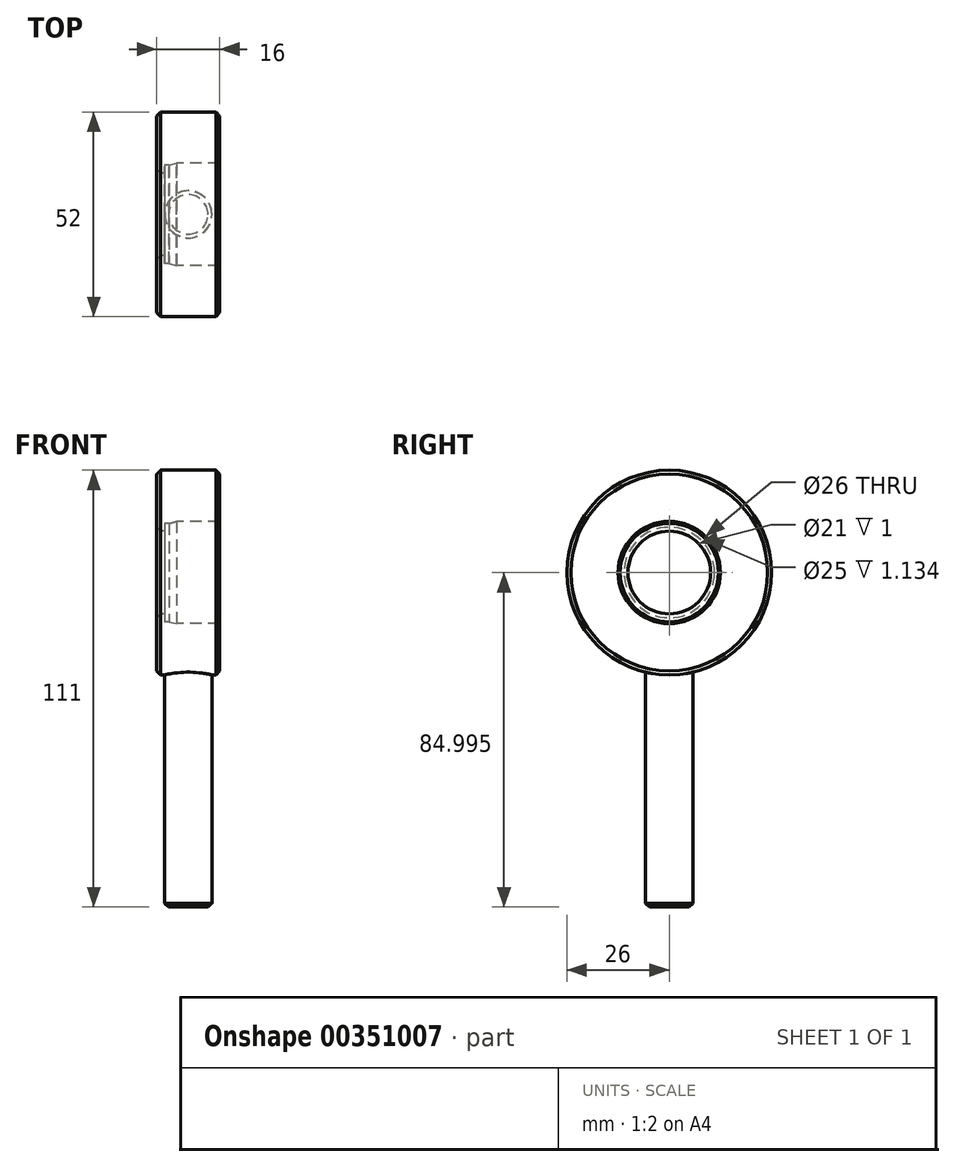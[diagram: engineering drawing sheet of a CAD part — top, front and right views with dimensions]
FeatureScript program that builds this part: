
annotation { "Feature Type Name" : "Feature", "Feature Type Description" : "" }
export const myFeature = defineFeature(function(context is Context, id is Id, definition is map)
    precondition{}
    {
        {
            var Q0;
            Q0=qCreatedBy(makeId("Front.planeOp"),FACE);
            var sketch = newSketch(context, id + "F0", { "sketchPlane" : qUnion([Q0])});
            skLineSegment(sketch, "E0", {"start": v(70.14, -4.23) * mm, "end": v(70.14, 46.77) * mm});
            skLineSegment(sketch, "E1", {"start": v(69.14, 45.77) * mm, "end": v(69.14, -4.23) * mm});
            skLineSegment(sketch, "E2", {"start": v(85.14, -4.23) * mm, "end": v(85.14, 45.77) * mm});
            skLineSegment(sketch, "E3", {"start": v(84.14, 46.77) * mm, "end": v(84.14, -4.23) * mm});
            skArc(sketch, "E4", {"start": v(29.78, -4.23) * mm, "mid": v(22.64, 46.77) * mm, "end": v(15.5, -4.23) * mm});
            skCircle(sketch, "E5", {"center": v(22.64, 20.77) * mm, "radius": 25 * mm});
            skLineSegment(sketch, "E6", {"start": v(22.64, -68.3) * mm, "end": v(22.64, 49.96) * mm});
            skLineSegment(sketch, "E7", {"start": v(-39.86, -4.23) * mm, "end": v(-39.86, 45.77) * mm});
            skLineSegment(sketch, "E8", {"start": v(-23.86, 45.77) * mm, "end": v(-23.86, -4.23) * mm});
            skArc(sketch, "E9", {"start": v(-79.22, -4.23) * mm, "mid": v(-86.36, 46.77) * mm, "end": v(-93.5, -4.23) * mm});
            skCircle(sketch, "E10", {"center": v(-86.36, 20.77) * mm, "radius": 25 * mm});
            skLineSegment(sketch, "E11", {"start": v(-86.36, -68.3) * mm, "end": v(-86.36, 50.51) * mm});
            skLineSegment(sketch, "E12", {"start": v(-7.6, 20.77) * mm, "end": v(53.07, 20.77) * mm});
            skCircle(sketch, "E13", {"center": v(-86.36, 20.77) * mm, "radius": 11.5 * mm});
            skLineSegment(sketch, "E14", {"start": v(-56.1, 20.77) * mm, "end": v(-117.02, 20.77) * mm});
            skLineSegment(sketch, "E15", {"start": v(-92.36, -63.23) * mm, "end": v(-92.36, -4.23) * mm});
            skLineSegment(sketch, "E16", {"start": v(-80.36, -4.23) * mm, "end": v(-80.36, -63.23) * mm});
            skLineSegment(sketch, "E17", {"start": v(-80.36, -63.23) * mm, "end": v(-81.36, -64.23) * mm});
            skLineSegment(sketch, "E18", {"start": v(-91.36, -64.23) * mm, "end": v(-92.36, -63.23) * mm});
            skLineSegment(sketch, "E19", {"start": v(-81.36, -64.23) * mm, "end": v(-91.36, -64.23) * mm});
            skLineSegment(sketch, "E20", {"start": v(-92.36, -63.23) * mm, "end": v(-80.36, -63.23) * mm});
            skCircle(sketch, "E21", {"center": v(-86.36, 20.77) * mm, "radius": 10.5 * mm});
            skCircle(sketch, "E22", {"center": v(-86.36, -9.23) * mm, "radius": 2 * mm});
            skLineSegment(sketch, "E23", {"start": v(-83.6, -9.23) * mm, "end": v(-89.12, -9.23) * mm});
            skLineSegment(sketch, "E24", {"start": v(-79.22, -4.23) * mm, "end": v(-93.5, -4.23) * mm});
            skLineSegment(sketch, "E25", {"start": v(16.64, -63.23) * mm, "end": v(16.64, -4.23) * mm});
            skLineSegment(sketch, "E26", {"start": v(28.64, -4.23) * mm, "end": v(28.64, -63.23) * mm});
            skLineSegment(sketch, "E27", {"start": v(-37.86, -63.23) * mm, "end": v(-37.86, -4.23) * mm});
            skLineSegment(sketch, "E28", {"start": v(-25.86, -4.23) * mm, "end": v(-25.86, -63.23) * mm});
            skLineSegment(sketch, "E29", {"start": v(-31.86, 2.77) * mm, "end": v(-31.86, -68.3) * mm});
            skLineSegment(sketch, "E30", {"start": v(-26.86, -64.23) * mm, "end": v(-25.86, -63.23) * mm});
            skLineSegment(sketch, "E31", {"start": v(-36.86, -64.23) * mm, "end": v(-26.86, -64.23) * mm});
            skLineSegment(sketch, "E32", {"start": v(-37.86, -63.23) * mm, "end": v(-36.86, -64.23) * mm});
            skLineSegment(sketch, "E33", {"start": v(-25.86, -63.23) * mm, "end": v(-37.86, -63.23) * mm});
            skLineSegment(sketch, "E34", {"start": v(28.64, -63.23) * mm, "end": v(27.64, -64.23) * mm});
            skLineSegment(sketch, "E35", {"start": v(17.64, -64.23) * mm, "end": v(16.64, -63.23) * mm});
            skLineSegment(sketch, "E36", {"start": v(27.64, -64.23) * mm, "end": v(17.64, -64.23) * mm});
            skLineSegment(sketch, "E37", {"start": v(16.64, -63.23) * mm, "end": v(28.64, -63.23) * mm});
            skLineSegment(sketch, "E38", {"start": v(-38.86, 31.27) * mm, "end": v(-38.86, 10.27) * mm});
            skLineSegment(sketch, "E39", {"start": v(-27.86, 33.27) * mm, "end": v(-27.86, 8.27) * mm});
            skLineSegment(sketch, "E40", {"start": v(-37.86, 8.27) * mm, "end": v(-37.86, 33.27) * mm});
            skLineSegment(sketch, "E41", {"start": v(-26.86, 33.77) * mm, "end": v(-26.86, 7.77) * mm});
            skLineSegment(sketch, "E42", {"start": v(-34.86, 7.77) * mm, "end": v(-34.86, 33.77) * mm});
            skLineSegment(sketch, "E43", {"start": v(-36.73, 8.27) * mm, "end": v(-34.86, 7.77) * mm});
            skLineSegment(sketch, "E44", {"start": v(-34.86, 7.77) * mm, "end": v(-26.86, 7.77) * mm});
            skLineSegment(sketch, "E45", {"start": v(-28.86, 0.27) * mm, "end": v(-29.36, 0.77) * mm});
            skLineSegment(sketch, "E46", {"start": v(-29.36, -4.23) * mm, "end": v(-29.36, -3.03) * mm});
            skLineSegment(sketch, "E47", {"start": v(-28.86, -3.03) * mm, "end": v(-28.86, 0.27) * mm});
            skLineSegment(sketch, "E48", {"start": v(-29.36, 0.77) * mm, "end": v(-29.36, -3.03) * mm});
            skLineSegment(sketch, "E49", {"start": v(-34.36, 0.77) * mm, "end": v(-34.86, 0.27) * mm});
            skLineSegment(sketch, "E50", {"start": v(-34.36, -3.03) * mm, "end": v(-34.36, -4.23) * mm});
            skLineSegment(sketch, "E51", {"start": v(-34.86, 0.27) * mm, "end": v(-34.86, -3.03) * mm});
            skLineSegment(sketch, "E52", {"start": v(-34.36, -3.03) * mm, "end": v(-34.36, 0.77) * mm});
            skLineSegment(sketch, "E53", {"start": v(-34.86, -3.03) * mm, "end": v(-28.86, -3.03) * mm});
            skLineSegment(sketch, "E54", {"start": v(-29.36, 0.77) * mm, "end": v(-34.36, 0.77) * mm});
            skLineSegment(sketch, "E55", {"start": v(-28.86, 0.27) * mm, "end": v(-34.86, 0.27) * mm});
            skLineSegment(sketch, "E56", {"start": v(-26.86, 7.77) * mm, "end": v(-23.86, 7.77) * mm});
            skLineSegment(sketch, "E57", {"start": v(-23.86, 9.77) * mm, "end": v(-27.86, 9.77) * mm});
            skLineSegment(sketch, "E58", {"start": v(-26.86, 8.27) * mm, "end": v(-23.86, 8.27) * mm});
            skLineSegment(sketch, "E59", {"start": v(-38.86, 10.27) * mm, "end": v(-37.86, 10.27) * mm});
            skLineSegment(sketch, "E60", {"start": v(-38.86, 10.27) * mm, "end": v(-39.86, 9.27) * mm});
            skLineSegment(sketch, "E61", {"start": v(-23.86, -4.23) * mm, "end": v(-39.86, -4.23) * mm});
            skLineSegment(sketch, "E62", {"start": v(-26.86, 8.27) * mm, "end": v(-37.86, 8.27) * mm});
            skLineSegment(sketch, "E63", {"start": v(-34.86, 33.77) * mm, "end": v(-36.73, 33.27) * mm});
            skLineSegment(sketch, "E64", {"start": v(-26.86, 33.77) * mm, "end": v(-34.86, 33.77) * mm});
            skLineSegment(sketch, "E65", {"start": v(-26.86, 33.77) * mm, "end": v(-23.86, 33.77) * mm});
            skLineSegment(sketch, "E66", {"start": v(-23.86, 33.27) * mm, "end": v(-26.86, 33.27) * mm});
            skLineSegment(sketch, "E67", {"start": v(-37.86, 33.27) * mm, "end": v(-26.86, 33.27) * mm});
            skLineSegment(sketch, "E68", {"start": v(-24.86, 20.27) * mm, "end": v(-24.86, 21.27) * mm});
            skLineSegment(sketch, "E69", {"start": v(-23.86, 20.27) * mm, "end": v(-24.86, 20.27) * mm});
            skLineSegment(sketch, "E70", {"start": v(-24.86, 21.27) * mm, "end": v(-23.86, 21.27) * mm});
            skLineSegment(sketch, "E71", {"start": v(-23.86, 31.77) * mm, "end": v(-27.86, 31.77) * mm});
            skLineSegment(sketch, "E72", {"start": v(-37.86, 31.27) * mm, "end": v(-38.86, 31.27) * mm});
            skLineSegment(sketch, "E73", {"start": v(-43.12, 20.77) * mm, "end": v(-19.9, 20.77) * mm});
            skLineSegment(sketch, "E74", {"start": v(-38.86, 31.27) * mm, "end": v(-39.86, 32.27) * mm});
            skCircle(sketch, "E75", {"center": v(22.64, 20.77) * mm, "radius": 10.5 * mm});
            skArc(sketch, "E76", {"start": v(10.15, 20.27) * mm, "mid": v(22.64, 8.27) * mm, "end": v(35.13, 20.27) * mm});
            skCircle(sketch, "E77", {"center": v(22.64, 20.77) * mm, "radius": 13 * mm});
            skCircle(sketch, "E78", {"center": v(22.64, -9.23) * mm, "radius": 2 * mm});
            skLineSegment(sketch, "E79", {"start": v(25.4, -9.23) * mm, "end": v(19.88, -9.23) * mm});
            skLineSegment(sketch, "E80", {"start": v(15.5, -4.23) * mm, "end": v(29.78, -4.23) * mm});
            skLineSegment(sketch, "E81", {"start": v(35.63, 20.27) * mm, "end": v(33.13, 20.27) * mm});
            skLineSegment(sketch, "E82", {"start": v(33.13, 21.27) * mm, "end": v(35.63, 21.27) * mm});
            skLineSegment(sketch, "E83", {"start": v(12.15, 21.27) * mm, "end": v(9.65, 21.27) * mm});
            skLineSegment(sketch, "E84", {"start": v(9.65, 20.27) * mm, "end": v(12.15, 20.27) * mm});
            skArc(sketch, "E85", {"start": v(35.13, 21.27) * mm, "mid": v(22.64, 33.27) * mm, "end": v(10.15, 21.27) * mm});
            skLineSegment(sketch, "E86", {"start": v(71.14, -63.23) * mm, "end": v(71.14, -4.23) * mm});
            skLineSegment(sketch, "E87", {"start": v(83.14, -4.23) * mm, "end": v(83.14, -63.23) * mm});
            skLineSegment(sketch, "E88", {"start": v(77.14, 2.77) * mm, "end": v(77.14, -68.3) * mm});
            skLineSegment(sketch, "E89", {"start": v(82.14, -64.23) * mm, "end": v(83.14, -63.23) * mm});
            skLineSegment(sketch, "E90", {"start": v(71.14, -63.23) * mm, "end": v(72.14, -64.23) * mm});
            skLineSegment(sketch, "E91", {"start": v(72.14, -64.23) * mm, "end": v(82.14, -64.23) * mm});
            skLineSegment(sketch, "E92", {"start": v(83.14, -63.23) * mm, "end": v(71.14, -63.23) * mm});
            skLineSegment(sketch, "E93", {"start": v(69.14, -4.23) * mm, "end": v(85.14, -4.23) * mm});
            skLineSegment(sketch, "E94", {"start": v(64.94, 20.77) * mm, "end": v(89.34, 20.77) * mm});
            skLineSegment(sketch, "E95", {"start": v(-2.36, 71.33) * mm, "end": v(47.64, 71.33) * mm});
            skLineSegment(sketch, "E96", {"start": v(47.64, 87.33) * mm, "end": v(-2.36, 87.33) * mm});
            skLineSegment(sketch, "E97", {"start": v(-3.36, 72.33) * mm, "end": v(48.64, 72.33) * mm});
            skLineSegment(sketch, "E98", {"start": v(48.64, 86.33) * mm, "end": v(-3.36, 86.33) * mm});
            skLineSegment(sketch, "E99", {"start": v(-7.6, 79.33) * mm, "end": v(53.07, 79.33) * mm});
            skLineSegment(sketch, "E100", {"start": v(-24.86, 46.77) * mm, "end": v(-23.86, 45.77) * mm});
            skLineSegment(sketch, "E101", {"start": v(-39.86, 45.77) * mm, "end": v(-38.86, 46.77) * mm});
            skLineSegment(sketch, "E102", {"start": v(-38.86, 46.77) * mm, "end": v(-24.86, 46.77) * mm});
            skLineSegment(sketch, "E103", {"start": v(22.64, 67.55) * mm, "end": v(22.64, 90.73) * mm});
            skLineSegment(sketch, "E104", {"start": v(-2.36, 87.33) * mm, "end": v(-3.36, 86.33) * mm});
            skLineSegment(sketch, "E105", {"start": v(-3.36, 72.33) * mm, "end": v(-2.36, 71.33) * mm});
            skLineSegment(sketch, "E106", {"start": v(-3.36, 86.33) * mm, "end": v(-3.36, 72.33) * mm});
            skLineSegment(sketch, "E107", {"start": v(85.14, 45.77) * mm, "end": v(84.14, 46.77) * mm});
            skLineSegment(sketch, "E108", {"start": v(70.14, 46.77) * mm, "end": v(69.14, 45.77) * mm});
            skLineSegment(sketch, "E109", {"start": v(84.14, 46.77) * mm, "end": v(70.14, 46.77) * mm});
            skLineSegment(sketch, "E110", {"start": v(48.64, 86.33) * mm, "end": v(47.64, 87.33) * mm});
            skLineSegment(sketch, "E111", {"start": v(47.64, 71.33) * mm, "end": v(48.64, 72.33) * mm});
            skLineSegment(sketch, "E112", {"start": v(48.64, 72.33) * mm, "end": v(48.64, 86.33) * mm});
            skSolve(sketch);
        }
        {
            var Q0;
            {var subQ3=sQuery(id+"F0.wireOp",EDGE,"E63");Q0=makeQuery(id+"F0.imprint","IMPRINT",FACE,{"disambiguationData":[TD([[makeQuery(id+"F0.imprint","IMPRINT",EDGE,{"derivedFrom":subQ3}),-1.0]])]});}
            var sketch = newSketch(context, id + "F1", { "sketchPlane" : qUnion([Q0])});
            skLineSegment(sketch, "E113.0.0", {"start": v(-39.86, 32.27) * mm, "end": v(-38.86, 31.27) * mm});
            skLineSegment(sketch, "E113.0.1", {"start": v(-38.86, 31.27) * mm, "end": v(-37.86, 31.27) * mm});
            skLineSegment(sketch, "E113.0.2", {"start": v(-37.86, 31.27) * mm, "end": v(-37.86, 33.27) * mm});
            skLineSegment(sketch, "E113.0.3", {"start": v(-37.86, 33.27) * mm, "end": v(-36.73, 33.27) * mm});
            skLineSegment(sketch, "E113.0.4", {"start": v(-36.73, 33.27) * mm, "end": v(-34.86, 33.77) * mm});
            skLineSegment(sketch, "E113.0.5", {"start": v(-34.86, 33.77) * mm, "end": v(-26.86, 33.77) * mm});
            skLineSegment(sketch, "E113.0.6", {"start": v(-26.86, 33.77) * mm, "end": v(-23.86, 33.77) * mm});
            skLineSegment(sketch, "E113.0.7", {"start": v(-23.86, 33.77) * mm, "end": v(-23.86, 45.77) * mm});
            skLineSegment(sketch, "E113.0.8", {"start": v(-23.86, 45.77) * mm, "end": v(-24.86, 46.77) * mm});
            skLineSegment(sketch, "E113.0.9", {"start": v(-24.86, 46.77) * mm, "end": v(-38.86, 46.77) * mm});
            skLineSegment(sketch, "E113.0.10", {"start": v(-38.86, 46.77) * mm, "end": v(-39.86, 45.77) * mm});
            skLineSegment(sketch, "E113.0.11", {"start": v(-39.86, 45.77) * mm, "end": v(-39.86, 32.27) * mm});
            skLineSegment(sketch, "E114.0", {"start": v(-43.12, 20.77) * mm, "end": v(-19.9, 20.77) * mm});
            skSolve(sketch);
        }
        {
            var Q0;
            Q0 = qSketchRegion(id + "F1", true);
            var Q1;
            Q1=sQuery(id+"F1.wireOp",EDGE,"E114.0");
            revolve(context, id + "F2", {"entities" : qUnion([Q0]), "axis" : qUnion([Q1]), "revolveType" : RevolveType.FULL});
        }
        {
            var Q0;
            Q0=qCreatedBy(makeId("Front.planeOp"),FACE);
            var sketch = newSketch(context, id + "F3", { "sketchPlane" : qUnion([Q0])});
            skLineSegment(sketch, "E115.0", {"start": v(-36.86, -64.23) * mm, "end": v(-26.86, -64.23) * mm});
            skLineSegment(sketch, "E116.0", {"start": v(-37.86, -63.23) * mm, "end": v(-36.86, -64.23) * mm});
            skLineSegment(sketch, "E117.0", {"start": v(-37.86, -63.23) * mm, "end": v(-37.86, -4.23) * mm});
            skLineSegment(sketch, "E118.0", {"start": v(-31.86, 2.77) * mm, "end": v(-31.86, -68.3) * mm});
            skSolve(sketch);
        }
        {
            var Q0;
            {var subQ5=sQuery(id+"F0.wireOp",EDGE,"E32");Q0=makeQuery(id+"F0.imprint","IMPRINT",FACE,{"disambiguationData":[TD([[makeQuery(id+"F0.imprint","IMPRINT",EDGE,{"derivedFrom":subQ5}),1.0]])]});}
            var Q1;
            {var subQ1=sQuery(id+"F0.wireOp",EDGE,"E27");Q1=makeQuery(id+"F0.imprint","IMPRINT",FACE,{"disambiguationData":[TD([[makeQuery(id+"F0.imprint","IMPRINT",EDGE,{"derivedFrom":subQ1}),-1.0]])]});}
            var Q2;
            Q2=sQuery(id+"F3.wireOp",EDGE,"E118.0");
            revolve(context, id + "F4", {"operationType" : NewBodyOperationType.ADD, "entities" : qUnion([Q0, Q1]), "axis" : qUnion([Q2]), "revolveType" : RevolveType.FULL});
        }
    });
